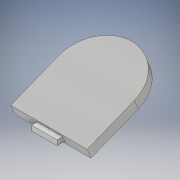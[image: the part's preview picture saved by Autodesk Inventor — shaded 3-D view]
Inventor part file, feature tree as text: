
AUTODESK INVENTOR PART (.ipt)
format: ipt  version: 2018 (Build 220112000, 112)  size: 134,656 bytes
history: native  units: in
note: dims shown in document units (in); Inventor stores cm internally (conversion verified against a paired STEP export)
features: sketch x4, extrude x2, plane x1
ambient origin geometry x8: Origin, YZ Plane, XZ Plane, XY Plane, X Axis, Y Axis, Z Axis, Center Point
bodies: Solid1 (feature_tree)
feature tree (7):
  extrude  "Extrusion1"  Depth=0.7874in
  sketch  "Sketch2"  dims[d2=1.9685in d3=0.0in d4=11.811in]
  plane  "Work Plane1"
  sketch  "Sketch3"  dims[d5=7.874in]
  extrude  "Extrusion2"  Depth=11.811in
  sketch  "Sketch1"  dims[d0=3.937in d1=0.7874in]
  sketch  "Sketch4"  dims[d6=11.811in d7=3.937in d8=0.7676in d9=4.3298in d10=1.5748in d11=0.0in]
